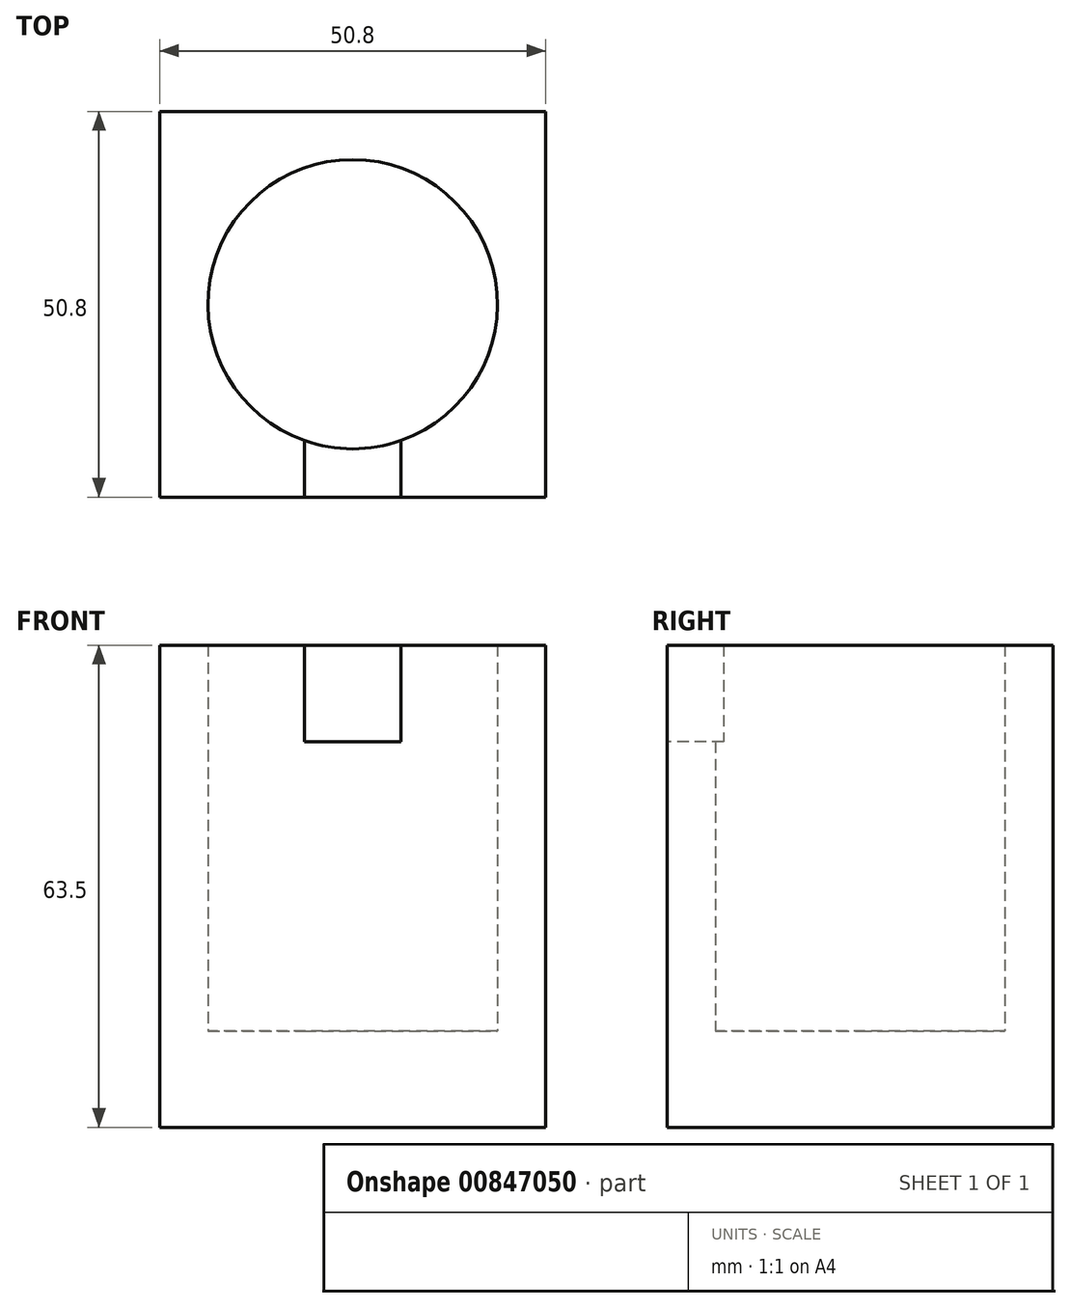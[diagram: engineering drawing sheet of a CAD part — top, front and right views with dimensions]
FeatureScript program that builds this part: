
annotation { "Feature Type Name" : "Feature", "Feature Type Description" : "" }
export const myFeature = defineFeature(function(context is Context, id is Id, definition is map)
    precondition{}
    {
        {
            var Q0;
            Q0=qCreatedBy(makeId("Top.planeOp"),FACE);
            var sketch = newSketch(context, id + "F0", { "sketchPlane" : qUnion([Q0])});
            skLineSegment(sketch, "E0.bottom", {"start": v(-50.8, 50.8) * mm, "end": v(0, 50.8) * mm});
            skLineSegment(sketch, "E0.top", {"start": v(-50.8, 0) * mm, "end": v(0, 0) * mm});
            skLineSegment(sketch, "E0.left", {"start": v(-50.8, 50.8) * mm, "end": v(-50.8, 0) * mm});
            skLineSegment(sketch, "E0.right", {"start": v(0, 50.8) * mm, "end": v(0, 0) * mm});
            skLineSegment(sketch, "E1", {"start": v(0, 25.4) * mm, "end": v(0, 0) * mm});
            skLineSegment(sketch, "E2", {"start": v(0, 0) * mm, "end": v(-25.4, 0) * mm});
            skCircle(sketch, "E3", {"center": v(-25.4, 25.4) * mm, "radius": 19.05 * mm});
            skSolve(sketch);
        }
        {
            var Q0;
            Q0=makeQuery(id+"F0.imprint","IMPRINT",FACE,{"disambiguationData":[TD([[makeQuery(id+"F0.imprint","IMPRINT",EDGE,{"derivedFrom":sQuery(id+"F0.wireOp",EDGE,"E0.bottom")}),-1.0]])]});
            extrude(context, id + "F1", {"entities" : qUnion([Q0]), "depth" : 63.5 * mm, "offsetDistance" : 25.4 * mm});
        }
        {
            var Q0;
            Q0=makeQuery(id+"F0.imprint","IMPRINT",FACE,{"disambiguationData":[TD([[makeQuery(id+"F0.imprint","IMPRINT",EDGE,{"derivedFrom":sQuery(id+"F0.wireOp",EDGE,"E3")}),1.0]])]});
            extrude(context, id + "F2", {"entities" : qUnion([Q0]), "operationType" : NewBodyOperationType.ADD, "depth" : 12.7 * mm, "offsetDistance" : 25.4 * mm});
        }
        {
            var Q0;
            Q0=makeQuery(id+"F1.opExtrude","SWEPT_FACE",FACE,{"disambiguationData":[OSD([sQuery(id+"F0.wireOp",EDGE,"E0.top"),sQuery(id+"F0.wireOp",EDGE,"E2")])]});
            var sketch = newSketch(context, id + "F3", { "sketchPlane" : qUnion([Q0])});
            skLineSegment(sketch, "E4", {"start": v(0, 63.5) * mm, "end": v(-25.4, 63.5) * mm});
            skLineSegment(sketch, "E5", {"start": v(-25.4, 63.5) * mm, "end": v(-19.05, 63.5) * mm});
            skLineSegment(sketch, "E6", {"start": v(-19.05, 63.5) * mm, "end": v(-25.4, 63.5) * mm});
            skLineSegment(sketch, "E7", {"start": v(-31.75, 63.5) * mm, "end": v(-25.4, 63.5) * mm});
            skLineSegment(sketch, "E8", {"start": v(-25.4, 63.5) * mm, "end": v(-25.4, 50.8) * mm});
            skLineSegment(sketch, "E9.top", {"start": v(-31.75, 50.8) * mm, "end": v(-25.4, 50.8) * mm});
            skLineSegment(sketch, "E9.left", {"start": v(-31.75, 63.5) * mm, "end": v(-31.75, 50.8) * mm});
            skLineSegment(sketch, "E10.bottom", {"start": v(-25.4, 50.8) * mm, "end": v(-19.05, 50.8) * mm});
            skLineSegment(sketch, "E10.right", {"start": v(-19.05, 50.8) * mm, "end": v(-19.05, 63.5) * mm});
            skLineSegment(sketch, "E11.bottom", {"start": v(-19.05, 50.8) * mm, "end": v(-31.75, 50.8) * mm});
            skLineSegment(sketch, "E11.top", {"start": v(-19.05, 63.5) * mm, "end": v(-31.75, 63.5) * mm});
            skLineSegment(sketch, "E11.right", {"start": v(-31.75, 50.8) * mm, "end": v(-31.75, 63.5) * mm});
            skSolve(sketch);
        }
        {
            var Q0;
            Q0=qSketchRegion(id+"F3",true);
            extrude(context, id + "F4", {"entities" : qUnion([Q0]), "operationType" : NewBodyOperationType.REMOVE, "oppositeDirection" : true, "depth" : 7.62 * mm, "offsetDistance" : 25.4 * mm});
        }
    });
